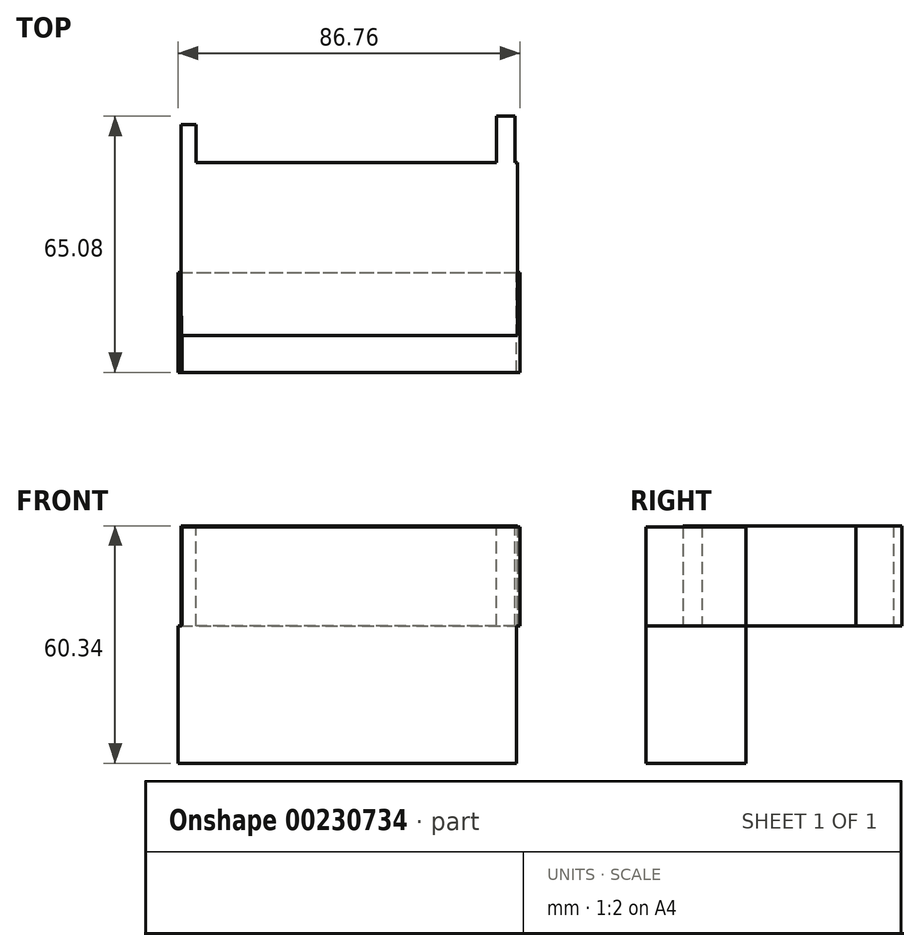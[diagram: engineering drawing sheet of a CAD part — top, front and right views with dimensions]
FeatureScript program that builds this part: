
annotation { "Feature Type Name" : "Feature", "Feature Type Description" : "" }
export const myFeature = defineFeature(function(context is Context, id is Id, definition is map)
    precondition{}
    {
        {
            var Q0;
            Q0=qCreatedBy(makeId("Top.planeOp"),FACE);
            var sketch = newSketch(context, id + "F0", { "sketchPlane" : qUnion([Q0])});
            skLineSegment(sketch, "E0.bottom", {"start": v(39.36, -16) * mm, "end": v(-45.98, -16) * mm});
            skLineSegment(sketch, "E0.top", {"start": v(39.36, 27.95) * mm, "end": v(-45.98, 27.95) * mm});
            skLineSegment(sketch, "E0.left", {"start": v(39.36, -16) * mm, "end": v(39.36, 27.95) * mm});
            skLineSegment(sketch, "E0.right", {"start": v(-45.98, -16) * mm, "end": v(-45.98, 27.95) * mm});
            skPoint(sketch, "E0.middle", {"position": v(-3.3, 5.97) * mm});
            skSolve(sketch);
        }
        {
            var Q0;
            Q0=qCreatedBy(makeId("Front.planeOp"),FACE);
            var sketch = newSketch(context, id + "F1", { "sketchPlane" : qUnion([Q0])});
            skLineSegment(sketch, "E1.bottom", {"start": v(-41.71, -32.22) * mm, "end": v(-45.98, -32.22) * mm});
            skLineSegment(sketch, "E1.top", {"start": v(-41.71, 0.21) * mm, "end": v(-45.98, 0.21) * mm});
            skLineSegment(sketch, "E1.left", {"start": v(-41.71, -32.22) * mm, "end": v(-41.71, 0.21) * mm});
            skLineSegment(sketch, "E1.right", {"start": v(-45.98, -32.22) * mm, "end": v(-45.98, 0.21) * mm});
            skPoint(sketch, "E1.middle", {"position": v(-43.85, -16) * mm});
            skLineSegment(sketch, "E2.bottom", {"start": v(34.24, -33.28) * mm, "end": v(38.94, -33.28) * mm});
            skLineSegment(sketch, "E2.top", {"start": v(34.24, 0) * mm, "end": v(38.94, 0) * mm});
            skLineSegment(sketch, "E2.left", {"start": v(34.24, -33.28) * mm, "end": v(34.24, 0) * mm});
            skLineSegment(sketch, "E2.right", {"start": v(38.94, -33.28) * mm, "end": v(38.94, 0) * mm});
            skPoint(sketch, "E2.middle", {"position": v(36.6, -16.64) * mm});
            skSolve(sketch);
        }
        {
            var Q0;
            Q0=qCreatedBy(makeId("Front.planeOp"),FACE);
            var sketch = newSketch(context, id + "F2", { "sketchPlane" : qUnion([Q0])});
            skLineSegment(sketch, "E3.bottom", {"start": v(38.83, -33.5) * mm, "end": v(34.14, -33.5) * mm});
            skLineSegment(sketch, "E3.top", {"start": v(38.83, 0.21) * mm, "end": v(34.14, 0.21) * mm});
            skLineSegment(sketch, "E3.left", {"start": v(38.83, -33.5) * mm, "end": v(38.83, 0.21) * mm});
            skLineSegment(sketch, "E3.right", {"start": v(34.14, -33.5) * mm, "end": v(34.14, 0.21) * mm});
            skPoint(sketch, "E3.middle", {"position": v(36.48, -16.64) * mm});
            skLineSegment(sketch, "E4.bottom", {"start": v(-42.03, -32.64) * mm, "end": v(-45.87, -32.64) * mm});
            skLineSegment(sketch, "E4.top", {"start": v(-42.03, 0.21) * mm, "end": v(-45.87, 0.21) * mm});
            skLineSegment(sketch, "E4.left", {"start": v(-42.03, -32.64) * mm, "end": v(-42.03, 0.21) * mm});
            skLineSegment(sketch, "E4.right", {"start": v(-45.87, -32.64) * mm, "end": v(-45.87, 0.21) * mm});
            skPoint(sketch, "E4.middle", {"position": v(-43.95, -16.22) * mm});
            skSolve(sketch);
        }
        {
            var Q0;
            Q0 = qSketchRegion(id + "F0", true);
            extrude(context, id + "F3", {"entities" : qUnion([Q0]), "depth" : 25.4 * mm});
        }
        {
            var Q0;
            Q0 = qSketchRegion(id + "F1", true);
            extrude(context, id + "F4", {"entities" : qUnion([Q0]), "operationType" : NewBodyOperationType.ADD, "depth" : 25.4 * mm});
        }
        {
            var Q0;
            Q0 = qSketchRegion(id + "F2", true);
            extrude(context, id + "F5", {"entities" : qUnion([Q0]), "operationType" : NewBodyOperationType.ADD, "depth" : 25.4 * mm});
        }
        {
            var Q0;
            Q0=qCreatedBy(makeId("Top.planeOp"),FACE);
            var sketch = newSketch(context, id + "F6", { "sketchPlane" : qUnion([Q0])});
            skLineSegment(sketch, "E5.bottom", {"start": v(-46.09, 37.55) * mm, "end": v(-42.25, 37.55) * mm});
            skLineSegment(sketch, "E5.top", {"start": v(-46.09, -11.1) * mm, "end": v(-42.25, -11.1) * mm});
            skLineSegment(sketch, "E5.left", {"start": v(-46.09, 37.55) * mm, "end": v(-46.09, -11.1) * mm});
            skLineSegment(sketch, "E5.right", {"start": v(-42.25, 37.55) * mm, "end": v(-42.25, -11.1) * mm});
            skPoint(sketch, "E5.middle", {"position": v(-44.17, 13.23) * mm});
            skLineSegment(sketch, "E6.bottom", {"start": v(38.83, 39.68) * mm, "end": v(34.14, 39.68) * mm});
            skLineSegment(sketch, "E6.top", {"start": v(38.83, -11.52) * mm, "end": v(34.14, -11.52) * mm});
            skLineSegment(sketch, "E6.left", {"start": v(38.83, 39.68) * mm, "end": v(38.83, -11.52) * mm});
            skLineSegment(sketch, "E6.right", {"start": v(34.14, 39.68) * mm, "end": v(34.14, -11.52) * mm});
            skPoint(sketch, "E6.middle", {"position": v(36.48, 14.08) * mm});
            skSolve(sketch);
        }
        {
            var Q0;
            Q0 = qSketchRegion(id + "F6", true);
            extrude(context, id + "F7", {"entities" : qUnion([Q0]), "operationType" : NewBodyOperationType.ADD, "depth" : 25.4 * mm});
        }
        {
            var Q0;
            Q0=qCreatedBy(makeId("Front.planeOp"),FACE);
            var sketch = newSketch(context, id + "F8", { "sketchPlane" : qUnion([Q0])});
            skLineSegment(sketch, "E7.bottom", {"start": v(40, 0) * mm, "end": v(-45.77, 0) * mm});
            skLineSegment(sketch, "E7.top", {"start": v(40, 25.18) * mm, "end": v(-45.77, 25.18) * mm});
            skLineSegment(sketch, "E7.left", {"start": v(40, 0) * mm, "end": v(40, 25.18) * mm});
            skLineSegment(sketch, "E7.right", {"start": v(-45.77, 0) * mm, "end": v(-45.77, 25.18) * mm});
            skPoint(sketch, "E7.middle", {"position": v(-2.88, 12.59) * mm});
            skSolve(sketch);
        }
        {
            var Q0;
            Q0 = qSketchRegion(id + "F8", true);
            extrude(context, id + "F9", {"entities" : qUnion([Q0]), "operationType" : NewBodyOperationType.ADD, "depth" : 25.4 * mm});
        }
        {
            var Q0;
            Q0=qCreatedBy(makeId("Front.planeOp"),FACE);
            var sketch = newSketch(context, id + "F10", { "sketchPlane" : qUnion([Q0])});
            skLineSegment(sketch, "E8.bottom", {"start": v(-46.75, 0) * mm, "end": v(39.16, 0) * mm});
            skLineSegment(sketch, "E8.top", {"start": v(-46.75, -34.94) * mm, "end": v(39.16, -34.94) * mm});
            skLineSegment(sketch, "E8.left", {"start": v(-46.75, 0) * mm, "end": v(-46.75, -34.94) * mm});
            skLineSegment(sketch, "E8.right", {"start": v(39.16, 0) * mm, "end": v(39.16, -34.94) * mm});
            skPoint(sketch, "E8.middle", {"position": v(-3.8, -17.47) * mm});
            skSolve(sketch);
        }
        {
            var Q0;
            Q0 = qSketchRegion(id + "F10", true);
            extrude(context, id + "F11", {"entities" : qUnion([Q0]), "operationType" : NewBodyOperationType.ADD, "depth" : 25.4 * mm});
        }
    });
